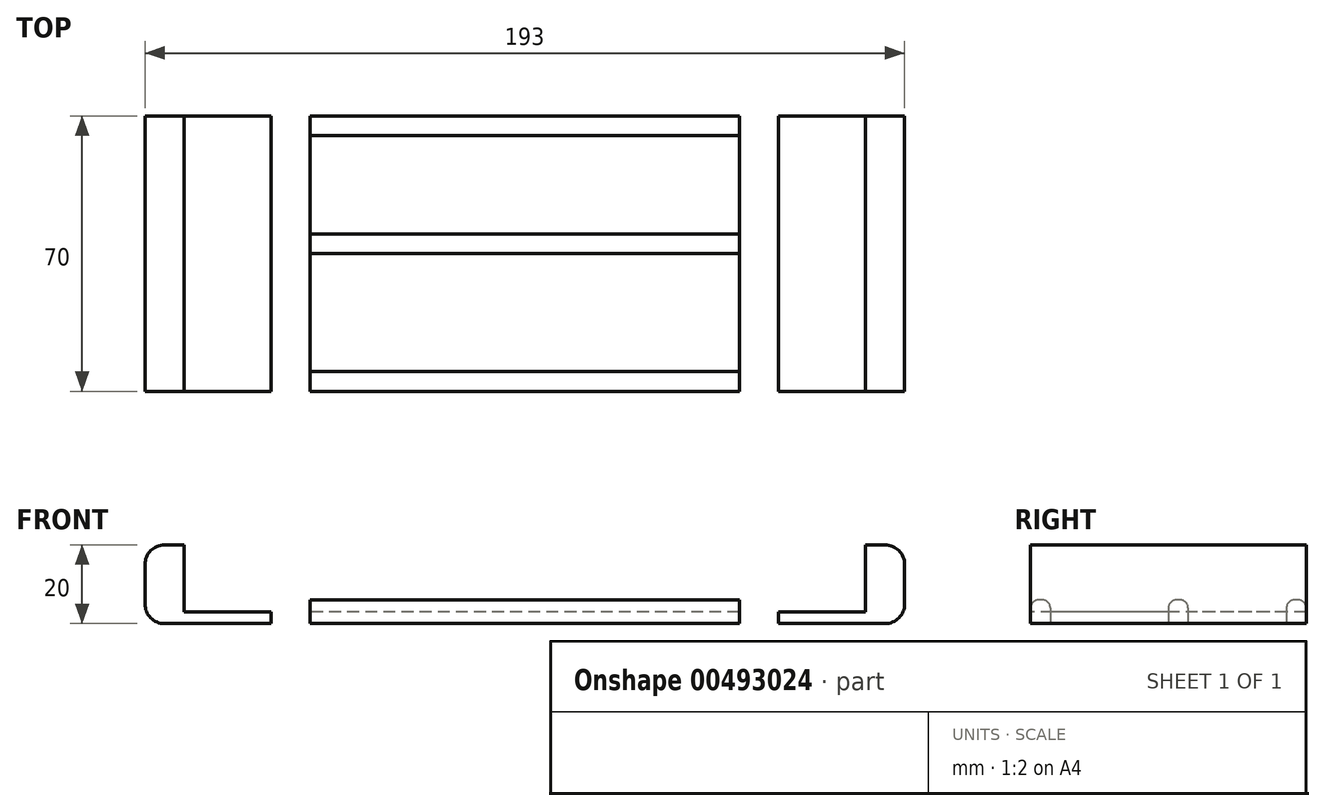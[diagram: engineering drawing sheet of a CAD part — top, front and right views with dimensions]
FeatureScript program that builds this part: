
annotation { "Feature Type Name" : "Feature", "Feature Type Description" : "" }
export const myFeature = defineFeature(function(context is Context, id is Id, definition is map)
    precondition{}
    {
        {
            var Q0;
            Q0=qCreatedBy(makeId("Top.planeOp"),FACE);
            var sketch = newSketch(context, id + "F0", { "sketchPlane" : qUnion([Q0])});
            skLineSegment(sketch, "E0", {"start": v(28.33, -30) * mm, "end": v(-100.67, -30) * mm});
            skLineSegment(sketch, "E1", {"start": v(-100.67, -30) * mm, "end": v(-122.67, -30) * mm});
            skLineSegment(sketch, "E2", {"start": v(28.33, -30) * mm, "end": v(50.33, -30) * mm});
            skLineSegment(sketch, "E3", {"start": v(-122.67, -30) * mm, "end": v(-122.67, 40) * mm});
            skLineSegment(sketch, "E4", {"start": v(-122.67, 40) * mm, "end": v(-100.67, 40) * mm});
            skLineSegment(sketch, "E5", {"start": v(-100.67, 40) * mm, "end": v(-100.67, -30) * mm});
            skLineSegment(sketch, "E6", {"start": v(50.33, -30) * mm, "end": v(50.33, 40) * mm});
            skLineSegment(sketch, "E7", {"start": v(50.33, 40) * mm, "end": v(28.33, 40) * mm});
            skLineSegment(sketch, "E8", {"start": v(28.33, -30) * mm, "end": v(28.33, 40) * mm});
            skLineSegment(sketch, "E9", {"start": v(28.33, 40) * mm, "end": v(-100.67, 40) * mm});
            skLineSegment(sketch, "E10.bottom", {"start": v(-122.67, 40) * mm, "end": v(-132.67, 40) * mm});
            skLineSegment(sketch, "E10.top", {"start": v(-122.67, -30) * mm, "end": v(-132.67, -30) * mm});
            skLineSegment(sketch, "E10.left", {"start": v(-122.67, 40) * mm, "end": v(-122.67, -30) * mm});
            skLineSegment(sketch, "E10.right", {"start": v(-132.67, 40) * mm, "end": v(-132.67, -30) * mm});
            skLineSegment(sketch, "E11.bottom", {"start": v(50.33, 40) * mm, "end": v(60.33, 40) * mm});
            skLineSegment(sketch, "E11.top", {"start": v(50.33, -30) * mm, "end": v(60.33, -30) * mm});
            skLineSegment(sketch, "E11.left", {"start": v(50.33, 40) * mm, "end": v(50.33, -30) * mm});
            skLineSegment(sketch, "E11.right", {"start": v(60.33, 40) * mm, "end": v(60.33, -30) * mm});
            skLineSegment(sketch, "E12.bottom", {"start": v(-100.67, 40) * mm, "end": v(-90.67, 40) * mm});
            skLineSegment(sketch, "E12.top", {"start": v(-100.67, -30) * mm, "end": v(-90.67, -30) * mm});
            skLineSegment(sketch, "E12.right", {"start": v(-90.67, 40) * mm, "end": v(-90.67, -30) * mm});
            skLineSegment(sketch, "E13.bottom", {"start": v(28.33, 40) * mm, "end": v(18.33, 40) * mm});
            skLineSegment(sketch, "E13.top", {"start": v(28.33, -30) * mm, "end": v(18.33, -30) * mm});
            skLineSegment(sketch, "E13.left", {"start": v(28.33, 40) * mm, "end": v(28.33, -30) * mm});
            skLineSegment(sketch, "E13.right", {"start": v(18.33, 40) * mm, "end": v(18.33, -30) * mm});
            skLineSegment(sketch, "E14", {"start": v(18.33, 5) * mm, "end": v(-90.67, 5) * mm});
            skLineSegment(sketch, "E15.0", {"start": v(18.33, 10) * mm, "end": v(-90.67, 10) * mm});
            skLineSegment(sketch, "E16", {"start": v(18.33, 40) * mm, "end": v(18.33, 35) * mm});
            skLineSegment(sketch, "E17", {"start": v(18.33, 35) * mm, "end": v(-90.67, 35) * mm});
            skLineSegment(sketch, "E18", {"start": v(18.33, -30) * mm, "end": v(18.33, -25) * mm});
            skLineSegment(sketch, "E19", {"start": v(18.33, -25) * mm, "end": v(-90.67, -25) * mm});
            skSolve(sketch);
        }
        {
            var Q0;
            Q0=makeQuery(id+"F0.imprint","IMPRINT",FACE,{"disambiguationData":[TD([[makeQuery(id+"F0.imprint","IMPRINT",EDGE,{"derivedFrom":sQuery(id+"F0.wireOp",EDGE,"E1")}),-1.0]])]});
            var Q1;
            Q1=makeQuery(id+"F0.imprint","IMPRINT",FACE,{"disambiguationData":[TD([[makeQuery(id+"F0.imprint","IMPRINT",EDGE,{"derivedFrom":sQuery(id+"F0.wireOp",EDGE,"E2")}),1.0]])]});
            var Q2;
            {var subQ0=sQuery(id+"F0.wireOp",EDGE,"E15.0");Q2=makeQuery(id+"F0.imprint","IMPRINT",FACE,{"disambiguationData":[TD([[makeQuery(id+"F0.imprint","IMPRINT",EDGE,{"derivedFrom":subQ0}),-1.0]])]});}
            var Q3;
            {var subQ0=sQuery(id+"F0.wireOp",EDGE,"E14");Q3=makeQuery(id+"F0.imprint","IMPRINT",FACE,{"disambiguationData":[TD([[makeQuery(id+"F0.imprint","IMPRINT",EDGE,{"derivedFrom":subQ0}),1.0]])]});}
            extrude(context, id + "F1", {"entities" : qUnion([Q0, Q1, Q2, Q3]), "depth" : 3 * mm});
        }
        {
            var Q0;
            Q0=makeQuery(id+"F0.imprint","IMPRINT",FACE,{"disambiguationData":[TD([[makeQuery(id+"F0.imprint","IMPRINT",EDGE,{"derivedFrom":sQuery(id+"F0.wireOp",EDGE,"E11.bottom")}),-1.0]])]});
            var Q1;
            Q1=makeQuery(id+"F0.imprint","IMPRINT",FACE,{"disambiguationData":[TD([[makeQuery(id+"F0.imprint","IMPRINT",EDGE,{"derivedFrom":sQuery(id+"F0.wireOp",EDGE,"E10.bottom")}),1.0]])]});
            var Q2;
            Q2=makeQuery(id+"F0.imprint","IMPRINT",FACE,{"disambiguationData":[TD([[makeQuery(id+"F0.imprint","IMPRINT",EDGE,{"derivedFrom":sQuery(id+"F0.wireOp",EDGE,"E12.bottom")}),-1.0]])]});
            var Q3;
            Q3=makeQuery(id+"F0.imprint","IMPRINT",FACE,{"disambiguationData":[TD([[makeQuery(id+"F0.imprint","IMPRINT",EDGE,{"derivedFrom":sQuery(id+"F0.wireOp",EDGE,"E13.bottom")}),1.0]])]});
            extrude(context, id + "F2", {"entities" : qUnion([Q0, Q1, Q2, Q3]), "operationType" : NewBodyOperationType.ADD, "depth" : 20 * mm});
        }
        {
            var Q0;
            {var subQ0=sQuery(id+"F0.wireOp",EDGE,"E14");Q0=makeQuery(id+"F0.imprint","IMPRINT",FACE,{"disambiguationData":[TD([[makeQuery(id+"F0.imprint","IMPRINT",EDGE,{"derivedFrom":subQ0}),-1.0]])]});}
            var Q1;
            {var subQ0=sQuery(id+"F0.wireOp",EDGE,"E0");Q1=makeQuery(id+"F0.imprint","IMPRINT",FACE,{"disambiguationData":[TD([[makeQuery(id+"F0.imprint","IMPRINT",EDGE,{"derivedFrom":subQ0}),-1.0]])]});}
            var Q2;
            {var subQ0=sQuery(id+"F0.wireOp",EDGE,"E9");Q2=makeQuery(id+"F0.imprint","IMPRINT",FACE,{"disambiguationData":[TD([[makeQuery(id+"F0.imprint","IMPRINT",EDGE,{"derivedFrom":subQ0}),1.0]])]});}
            extrude(context, id + "F3", {"entities" : qUnion([Q0, Q1, Q2]), "depth" : 6 * mm});
        }
        {
            var Q0;
            Q0=makeQuery(id+"F2.opExtrude","CAP_EDGE",EDGE,{"disambiguationData":[OSD([sQuery(id+"F0.wireOp",EDGE,"E11.left")])],"isStart":false});
            var Q1;
            Q1=makeQuery(id+"F2.opExtrude","CAP_EDGE",EDGE,{"disambiguationData":[OSD([sQuery(id+"F0.wireOp",EDGE,"E13.left")])],"isStart":false});
            var Q2;
            Q2=makeQuery(id+"F2.opExtrude","CAP_EDGE",EDGE,{"disambiguationData":[OSD([sQuery(id+"F0.wireOp",EDGE,"E5")])],"isStart":false});
            var Q3;
            Q3=makeQuery(id+"F2.opExtrude","CAP_EDGE",EDGE,{"disambiguationData":[OSD([sQuery(id+"F0.wireOp",EDGE,"E10.left")])],"isStart":false});
            var Q4;
            Q4=makeQuery(id+"F2.opExtrude","CAP_EDGE",EDGE,{"disambiguationData":[OSD([sQuery(id+"F0.wireOp",EDGE,"E10.right")])],"isStart":false});
            var Q5;
            Q5=makeQuery(id+"F2.opExtrude","CAP_EDGE",EDGE,{"disambiguationData":[OSD([sQuery(id+"F0.wireOp",EDGE,"E12.right")])],"isStart":false});
            var Q6;
            Q6=makeQuery(id+"F2.opExtrude","CAP_EDGE",EDGE,{"disambiguationData":[OSD([sQuery(id+"F0.wireOp",EDGE,"E13.right")])],"isStart":false});
            var Q7;
            Q7=makeQuery(id+"F2.opExtrude","CAP_EDGE",EDGE,{"disambiguationData":[OSD([sQuery(id+"F0.wireOp",EDGE,"E11.right")])],"isStart":false});
            fillet(context, id + "F4", {"entities" : qUnion([Q0, Q1, Q2, Q3, Q4, Q5, Q6, Q7]), "radius" : 5 * mm, "tangentPropagation" : true, "allowEdgeOverflow" : false});
        }
        {
            var Q0;
            Q0=makeQuery(id+"F2.opExtrude","CAP_EDGE",EDGE,{"disambiguationData":[OSD([sQuery(id+"F0.wireOp",EDGE,"E10.right")])],"isStart":true});
            var Q1;
            Q1=makeQuery(id+"F2.opExtrude","CAP_EDGE",EDGE,{"disambiguationData":[OSD([sQuery(id+"F0.wireOp",EDGE,"E11.right")])],"isStart":true});
            fillet(context, id + "F5", {"entities" : qUnion([Q0, Q1]), "radius" : 5 * mm, "tangentPropagation" : true, "allowEdgeOverflow" : false});
        }
        {
            var Q0;
            Q0=makeQuery(id+"F3.opExtrude","CAP_EDGE",EDGE,{"disambiguationData":[OSD([sQuery(id+"F0.wireOp",EDGE,"E14")])],"isStart":false});
            var Q1;
            Q1=makeQuery(id+"F3.opExtrude","CAP_EDGE",EDGE,{"disambiguationData":[OSD([sQuery(id+"F0.wireOp",EDGE,"E15.0")])],"isStart":false});
            var Q2;
            Q2=makeQuery(id+"F3.opExtrude","CAP_EDGE",EDGE,{"disambiguationData":[OSD([sQuery(id+"F0.wireOp",EDGE,"E0")])],"isStart":false});
            var Q3;
            Q3=makeQuery(id+"F3.opExtrude","CAP_EDGE",EDGE,{"disambiguationData":[OSD([sQuery(id+"F0.wireOp",EDGE,"E9")])],"isStart":false});
            var Q4;
            Q4=makeQuery(id+"F3.opExtrude","CAP_EDGE",EDGE,{"disambiguationData":[OSD([sQuery(id+"F0.wireOp",EDGE,"E17")])],"isStart":false});
            var Q5;
            Q5=makeQuery(id+"F3.opExtrude","CAP_EDGE",EDGE,{"disambiguationData":[OSD([sQuery(id+"F0.wireOp",EDGE,"E19")])],"isStart":false});
            fillet(context, id + "F6", {"entities" : qUnion([Q0, Q1, Q2, Q3, Q4, Q5]), "radius" : 2 * mm, "tangentPropagation" : true, "allowEdgeOverflow" : false});
        }
    });
